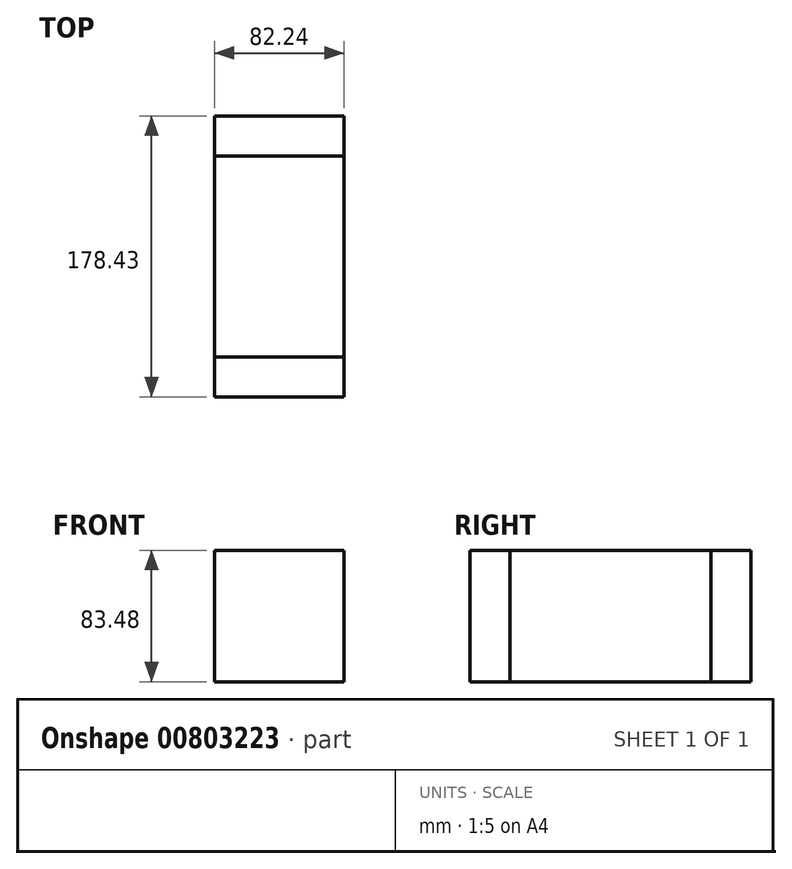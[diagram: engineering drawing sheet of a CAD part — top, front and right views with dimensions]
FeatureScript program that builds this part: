
annotation { "Feature Type Name" : "Feature", "Feature Type Description" : "" }
export const myFeature = defineFeature(function(context is Context, id is Id, definition is map)
    precondition{}
    {
        {
            var Q0;
            Q0=qCreatedBy(makeId("Front.planeOp"),FACE);
            var sketch = newSketch(context, id + "F0", { "sketchPlane" : qUnion([Q0])});
            skLineSegment(sketch, "E0.bottom", {"start": v(28.42, 29.04) * mm, "end": v(-28.42, 29.04) * mm});
            skLineSegment(sketch, "E0.top", {"start": v(28.42, -29.04) * mm, "end": v(-28.42, -29.04) * mm});
            skLineSegment(sketch, "E0.left", {"start": v(28.42, 29.04) * mm, "end": v(28.42, -29.04) * mm});
            skLineSegment(sketch, "E0.right", {"start": v(-28.42, 29.04) * mm, "end": v(-28.42, -29.04) * mm});
            skPoint(sketch, "E0.middle", {"position": v(0, 0) * mm});
            skSolve(sketch);
        }
        {
            var Q0;
            Q0=makeQuery(id+"F0.imprint","IMPRINT",FACE,{"disambiguationData":[TD([[makeQuery(id+"F0.imprint","IMPRINT",EDGE,{"derivedFrom":sQuery(id+"F0.wireOp",EDGE,"E0.bottom")}),1.0]])]});
            extrude(context, id + "F1", {"entities" : qUnion([Q0]), "oppositeDirection" : true, "depth" : 64.04 * mm, "offsetDistance" : 25.4 * mm});
        }
        {
            var Q0;
            Q0=makeQuery(id+"F1.opExtrude","CAP_FACE",FACE,{"disambiguationData":[OSD([sQuery(id+"F0.wireOp",EDGE,"E0.bottom"),sQuery(id+"F0.wireOp",EDGE,"E0.top"),sQuery(id+"F0.wireOp",EDGE,"E0.left"),sQuery(id+"F0.wireOp",EDGE,"E0.right")])],"isStart":true});
            extrude(context, id + "F2", {"entities" : qUnion([Q0]), "operationType" : NewBodyOperationType.ADD, "depth" : 63.6 * mm, "offsetDistance" : 25.4 * mm});
        }
        {
            var Q0;
            {var subQ0=sQuery(id+"F0.wireOp",EDGE,"E0.bottom");Q0=makeQuery(id+"F2.boolean.opBoolean","MERGE",FACE,{"derivedFrom":[makeQuery(id+"F1.opExtrude","SWEPT_FACE",FACE,{"disambiguationData":[OSD([subQ0])]}),makeQuery(id+"F2.opExtrude","SWEPT_FACE",FACE,{"disambiguationData":[OSD([subQ0])]})]});}
            extrude(context, id + "F3", {"entities" : qUnion([Q0]), "operationType" : NewBodyOperationType.ADD, "depth" : 25.4 * mm, "offsetDistance" : 25.4 * mm});
        }
        {
            var Q0;
            {var subQ0=sQuery(id+"F0.wireOp",EDGE,"E0.right");Q0=makeQuery(id+"F3.boolean.opBoolean","MERGE",FACE,{"derivedFrom":[makeQuery(id+"F2.boolean.opBoolean","MERGE",FACE,{"derivedFrom":[makeQuery(id+"F1.opExtrude","SWEPT_FACE",FACE,{"disambiguationData":[OSD([subQ0])]}),makeQuery(id+"F2.opExtrude","SWEPT_FACE",FACE,{"disambiguationData":[OSD([subQ0])]})]}),makeQuery(id+"F3.opExtrude","SWEPT_FACE",FACE,{"disambiguationData":[OSD([sQuery(id+"F0.wireOp",EDGE,"E0.bottom"),subQ0])]})]});}
            extrude(context, id + "F4", {"entities" : qUnion([Q0]), "operationType" : NewBodyOperationType.ADD, "depth" : 25.4 * mm, "offsetDistance" : 25.4 * mm});
        }
        {
            var Q0;
            {var subQ0=sQuery(id+"F0.wireOp",EDGE,"E0.right");var subQ1=sQuery(id+"F0.wireOp",EDGE,"E0.bottom");Q0=makeQuery(id+"F4.boolean.opBoolean","MERGE",FACE,{"derivedFrom":[makeQuery(id+"F3.boolean.opBoolean","MERGE",FACE,{"derivedFrom":[makeQuery(id+"F2.opExtrude","CAP_FACE",FACE,{"disambiguationData":[OSD([subQ1,sQuery(id+"F0.wireOp",EDGE,"E0.top"),sQuery(id+"F0.wireOp",EDGE,"E0.left"),subQ0])],"isStart":false}),makeQuery(id+"F3.opExtrude","SWEPT_FACE",FACE,{"disambiguationData":[OSD([subQ1]),TDD([makeQuery(id+"F2.opExtrude","CAP_EDGE",EDGE,{"disambiguationData":[OSD([subQ1])],"isStart":false})])]})]}),makeQuery(id+"F4.opExtrude","SWEPT_FACE",FACE,{"disambiguationData":[OSD([subQ1,subQ0]),TDD([makeQuery(id+"F3.boolean.opBoolean","MERGE",EDGE,{"derivedFrom":[makeQuery(id+"F2.opExtrude","CAP_EDGE",EDGE,{"disambiguationData":[OSD([subQ0])],"isStart":false}),makeQuery(id+"F3.opExtrude","SWEPT_EDGE",EDGE,{"disambiguationData":[OSD([subQ1,subQ0]),TDD([makeQuery(id+"F2.opExtrude","CAP_VERTEX",VERTEX,{"disambiguationData":[OSD([subQ1,subQ0])],"isStart":false})])]})]})])]})]});}
            extrude(context, id + "F5", {"entities" : qUnion([Q0]), "depth" : 25.4 * mm, "offsetDistance" : 25.4 * mm});
        }
        {
            var Q0;
            {var subQ0=sQuery(id+"F0.wireOp",EDGE,"E0.right");var subQ1=sQuery(id+"F0.wireOp",EDGE,"E0.bottom");Q0=makeQuery(id+"F4.boolean.opBoolean","MERGE",FACE,{"derivedFrom":[makeQuery(id+"F3.boolean.opBoolean","MERGE",FACE,{"derivedFrom":[makeQuery(id+"F1.opExtrude","CAP_FACE",FACE,{"disambiguationData":[OSD([subQ1,sQuery(id+"F0.wireOp",EDGE,"E0.top"),sQuery(id+"F0.wireOp",EDGE,"E0.left"),subQ0])],"isStart":false}),makeQuery(id+"F3.opExtrude","SWEPT_FACE",FACE,{"disambiguationData":[OSD([subQ1]),TDD([makeQuery(id+"F1.opExtrude","CAP_EDGE",EDGE,{"disambiguationData":[OSD([subQ1])],"isStart":false})])]})]}),makeQuery(id+"F4.opExtrude","SWEPT_FACE",FACE,{"disambiguationData":[OSD([subQ1,subQ0]),TDD([makeQuery(id+"F3.boolean.opBoolean","MERGE",EDGE,{"derivedFrom":[makeQuery(id+"F1.opExtrude","CAP_EDGE",EDGE,{"disambiguationData":[OSD([subQ0])],"isStart":false}),makeQuery(id+"F3.opExtrude","SWEPT_EDGE",EDGE,{"disambiguationData":[OSD([subQ1,subQ0]),TDD([makeQuery(id+"F1.opExtrude","CAP_VERTEX",VERTEX,{"disambiguationData":[OSD([subQ1,subQ0])],"isStart":false})])]})]})])]})]});}
            extrude(context, id + "F6", {"entities" : qUnion([Q0]), "depth" : 25.4 * mm, "offsetDistance" : 25.4 * mm});
        }
    });
